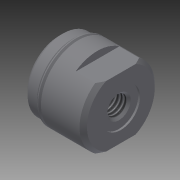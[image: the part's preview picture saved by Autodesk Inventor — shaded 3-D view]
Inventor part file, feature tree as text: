
AUTODESK INVENTOR PART (.ipt)
format: ipt  version: 2013 (Build 170138000, 138)  size: 210,944 bytes
history: native  units: in
note: dims shown in document units (in); Inventor stores cm internally (conversion verified against a paired STEP export)
features: other x112, sketch x5, revolve x2, hole x2, extrude x1
ambient origin geometry x8: Origin, YZ Plane, XZ Plane, XY Plane, X Axis, Y Axis, Z Axis, Center Point
bodies: Solid1 (feature_tree)
feature tree (122):
  revolve  "Revolution1"  [1 undecoded]
  hole  "Drilling 1"  [1 undecoded]
  hole  "Drilling 2"  [1 undecoded]
  extrude  "Extrusion1"  [1 undecoded]
  revolve  "Revolution2"  [1 undecoded]
  other  "cut1_XY"
  other  "cut1_YZ"
  other  "cut1_ZX"
  other  "cut1_X"
  other  "cut1_Y"
  other  "cut1_Z"
  other  "cut1_Center"
  other  "cut2_XY"
  other  "cut2_YZ"
  other  "cut2_ZX"
  other  "cut2_X"
  other  "cut2_Y"
  other  "cut2_Z"
  other  "cut2_Center"
  other  "to_tube_XY"
  other  "to_tube_YZ"
  other  "to_tube_ZX"
  other  "to_tube_X"
  other  "to_tube_Y"
  other  "to_tube_Z"
  other  "to_tube_Center"
  other  "lovra_XY"
  other  "lovra_YZ"
  other  "lovra_ZX"
  other  "lovra_X"
  other  "lovra_Y"
  other  "lovra_Z"
  other  "lovra_Center"
  other  "to_nut_XY"
  other  "to_nut_YZ"
  other  "to_nut_ZX"
  other  "to_nut_X"
  other  "to_nut_Y"
  other  "to_nut_Z"
  other  "to_nut_Center"
  other  "lovra1_XY"
  other  "lovra1_YZ"
  other  "lovra1_ZX"
  other  "lovra1_X"
  other  "lovra1_Y"
  other  "lovra1_Z"
  other  "lovra1_Center"
  other  "lovra2_XY"
  other  "lovra2_YZ"
  other  "lovra2_ZX"
  other  "lovra2_X"
  other  "lovra2_Y"
  other  "lovra2_Z"
  other  "lovra2_Center"
  other  "lovra3_XY"
  other  "lovra3_YZ"
  other  "lovra3_ZX"
  other  "lovra3_X"
  other  "lovra3_Y"
  other  "lovra3_Z"
  other  "lovra3_Center"
  other  "olen_XY"
  other  "olen_YZ"
  other  "olen_ZX"
  other  "olen_X"
  other  "olen_Y"
  other  "olen_Z"
  other  "olen_Center"
  other  "cutf1_XY"
  other  "cutf1_YZ"
  other  "cutf1_ZX"
  other  "cutf1_X"
  other  "cutf1_Y"
  other  "cutf1_Z"
  other  "cutf1_Center"
  other  "cutf2_XY"
  other  "cutf2_YZ"
  other  "cutf2_ZX"
  other  "cutf2_X"
  other  "cutf2_Y"
  other  "cutf2_Z"
  other  "cutf2_Center"
  other  "lovra21_XY"
  other  "lovra21_YZ"
  other  "lovra21_ZX"
  other  "lovra21_X"
  other  "lovra21_Y"
  other  "lovra21_Z"
  other  "lovra21_Center"
  other  "lovra22_XY"
  other  "lovra22_YZ"
  other  "lovra22_ZX"
  other  "lovra22_X"
  other  "lovra22_Y"
  other  "lovra22_Z"
  other  "lovra22_Center"
  other  "to_pin_XY"
  other  "to_pin_YZ"
  other  "to_pin_ZX"
  other  "to_pin_X"
  other  "to_pin_Y"
  other  "to_pin_Z"
  other  "to_pin_Center"
  other  "mbr_XY"
  other  "mbr_YZ"
  other  "mbr_ZX"
  other  "mbr_X"
  other  "mbr_Y"
  other  "mbr_Z"
  other  "mbr_Center"
  other  "to_nut1_XY"
  other  "to_nut1_YZ"
  other  "to_nut1_ZX"
  other  "to_nut1_X"
  other  "to_nut1_Y"
  other  "to_nut1_Z"
  other  "to_nut1_Center"
  sketch  "Sketch_1"  dims[d0=360.0deg]
  sketch  "Sketch2"  dims[d1=0.312in d2=0.75in d3=0.375in d4=0.25in d5=0.5635in d6=0.015in d7=0.0in]
  sketch  "Sketch3"  dims[d8=0.156in d9=0.2in d10=0.19in d11=0.25in d12=90.0deg d13=0.485in d14=0.0in d15=0.19in d16=0.0in]
  sketch  "Sketch_5"  dims[d17=360.0deg]
  sketch  "Sketch_24"
note: 5 required parameter values undecoded (feature->parameter linkage not recoverable at this tier; creation-order binding heuristic only, values carry confidence <= 0.55)